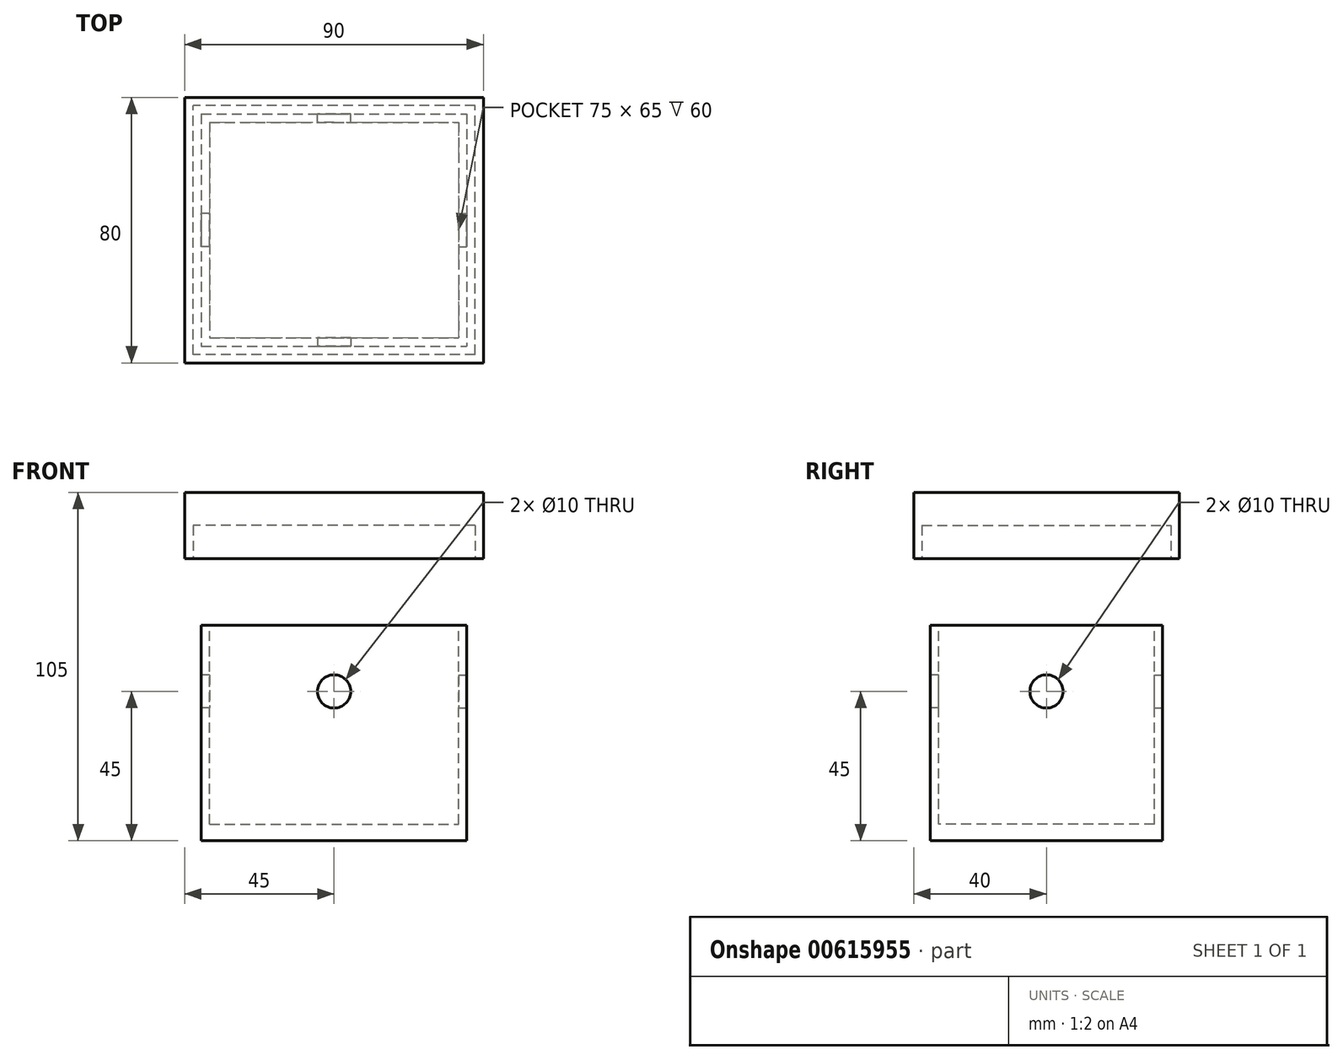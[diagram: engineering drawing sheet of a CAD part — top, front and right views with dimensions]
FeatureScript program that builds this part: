
annotation { "Feature Type Name" : "Feature", "Feature Type Description" : "" }
export const myFeature = defineFeature(function(context is Context, id is Id, definition is map)
    precondition{}
    {
        {
            var Q0;
            Q0=qCreatedBy(makeId("Top.planeOp"),FACE);
            var sketch = newSketch(context, id + "F0", { "sketchPlane" : qUnion([Q0])});
            skLineSegment(sketch, "E0.bottom", {"start": v(-40, 35) * mm, "end": v(40, 35) * mm});
            skLineSegment(sketch, "E0.top", {"start": v(-40, -35) * mm, "end": v(40, -35) * mm});
            skLineSegment(sketch, "E0.left", {"start": v(-40, 35) * mm, "end": v(-40, -35) * mm});
            skLineSegment(sketch, "E0.right", {"start": v(40, 35) * mm, "end": v(40, -35) * mm});
            skPoint(sketch, "E0.middle", {"position": v(0, 0) * mm});
            skLineSegment(sketch, "E1.bottom", {"start": v(-26.5, 26.5) * mm, "end": v(26.5, 26.5) * mm});
            skLineSegment(sketch, "E1.top", {"start": v(-26.5, -26.5) * mm, "end": v(26.5, -26.5) * mm});
            skLineSegment(sketch, "E1.left", {"start": v(-26.5, 26.5) * mm, "end": v(-26.5, -26.5) * mm});
            skLineSegment(sketch, "E1.right", {"start": v(26.5, 26.5) * mm, "end": v(26.5, -26.5) * mm});
            skSolve(sketch);
        }
        {
            var Q0;
            Q0=makeQuery(id+"F0.imprint","IMPRINT",FACE,{"disambiguationData":[TD([[makeQuery(id+"F0.imprint","IMPRINT",EDGE,{"derivedFrom":sQuery(id+"F0.wireOp",EDGE,"E1.bottom")}),-1.0]])]});
            var Q1;
            Q1=makeQuery(id+"F0.imprint","IMPRINT",FACE,{"disambiguationData":[TD([[makeQuery(id+"F0.imprint","IMPRINT",EDGE,{"derivedFrom":sQuery(id+"F0.wireOp",EDGE,"E0.bottom")}),-1.0]])]});
            extrude(context, id + "F1", {"entities" : qUnion([Q0, Q1]), "oppositeDirection" : true, "depth" : 5 * mm, "offsetDistance" : 25 * mm});
        }
        {
            var Q0;
            Q0=makeQuery(id+"F0.imprint","IMPRINT",FACE,{"disambiguationData":[TD([[makeQuery(id+"F0.imprint","IMPRINT",EDGE,{"derivedFrom":sQuery(id+"F0.wireOp",EDGE,"E0.bottom")}),-1.0]])]});
            extrude(context, id + "F2", {"entities" : qUnion([Q0]), "operationType" : NewBodyOperationType.ADD, "depth" : 60 * mm, "offsetDistance" : 25 * mm});
        }
        {
            var Q0;
            Q0=makeQuery(id+"F2.opExtrude","CAP_FACE",FACE,{"disambiguationData":[OSD([sQuery(id+"F0.wireOp",EDGE,"E0.bottom"),sQuery(id+"F0.wireOp",EDGE,"E0.top"),sQuery(id+"F0.wireOp",EDGE,"E0.left"),sQuery(id+"F0.wireOp",EDGE,"E0.right"),sQuery(id+"F0.wireOp",EDGE,"E1.bottom"),sQuery(id+"F0.wireOp",EDGE,"E1.top"),sQuery(id+"F0.wireOp",EDGE,"E1.left"),sQuery(id+"F0.wireOp",EDGE,"E1.right")])],"isStart":false});
            var sketch = newSketch(context, id + "F3", { "sketchPlane" : qUnion([Q0])});
            skLineSegment(sketch, "E2.bottom", {"start": v(45, 40) * mm, "end": v(-45, 40) * mm});
            skLineSegment(sketch, "E2.top", {"start": v(45, -40) * mm, "end": v(-45, -40) * mm});
            skLineSegment(sketch, "E2.left", {"start": v(45, 40) * mm, "end": v(45, -40) * mm});
            skLineSegment(sketch, "E2.right", {"start": v(-45, 40) * mm, "end": v(-45, -40) * mm});
            skPoint(sketch, "E2.middle", {"position": v(0, 0) * mm});
            skSolve(sketch);
        }
        {
            var Q0;
            Q0 = qSketchRegion(id + "F3", true);
            extrude(context, id + "F4", {"entities" : qUnion([Q0]), "operationType" : NewBodyOperationType.ADD, "depth" : 40 * mm, "offsetDistance" : 25 * mm});
        }
        {
            var Q0;
            Q0=makeQuery(id+"F3.imprint","IMPRINT",FACE,{"disambiguationData":[TD([[makeQuery(id+"F3.imprint","IMPRINT",EDGE,{"derivedFrom":sQuery(id+"F3.wireOp",EDGE,"E2.bottom")}),1.0]])]});
            var Q1;
            Q1 = qSketchRegion(id + "F3", true);
            extrude(context, id + "F5", {"entities" : qUnion([Q0, Q1]), "operationType" : NewBodyOperationType.REMOVE, "depth" : 20 * mm, "offsetDistance" : 25 * mm});
        }
        {
            var Q0;
            Q0=makeQuery(id+"F5.boolean.opBoolean","COPY",FACE,{"derivedFrom":makeQuery(id+"F5.opExtrude","CAP_FACE",FACE,{"disambiguationData":[OSD([sQuery(id+"F3.wireOp",EDGE,"E2.bottom"),sQuery(id+"F3.wireOp",EDGE,"E2.top"),sQuery(id+"F3.wireOp",EDGE,"E2.left"),sQuery(id+"F3.wireOp",EDGE,"E2.right")])],"isStart":false})});
            var sketch = newSketch(context, id + "F6", { "sketchPlane" : qUnion([Q0])});
            skLineSegment(sketch, "E3.bottom", {"start": v(42.5, 37.5) * mm, "end": v(-42.5, 37.5) * mm});
            skLineSegment(sketch, "E3.top", {"start": v(42.5, -37.5) * mm, "end": v(-42.5, -37.5) * mm});
            skLineSegment(sketch, "E3.left", {"start": v(42.5, 37.5) * mm, "end": v(42.5, -37.5) * mm});
            skLineSegment(sketch, "E3.right", {"start": v(-42.5, 37.5) * mm, "end": v(-42.5, -37.5) * mm});
            skPoint(sketch, "E3.middle", {"position": v(0, 0) * mm});
            skSolve(sketch);
        }
        {
            var Q0;
            Q0 = qSketchRegion(id + "F6", true);
            extrude(context, id + "F7", {"entities" : qUnion([Q0]), "operationType" : NewBodyOperationType.REMOVE, "oppositeDirection" : true, "depth" : 10 * mm, "offsetDistance" : 25 * mm});
        }
        {
            var Q0;
            Q0=makeQuery(id+"F3.imprint","IMPRINT",FACE,{"disambiguationData":[TD([[makeQuery(id+"F3.imprint","IMPRINT",EDGE,{"derivedFrom":makeQuery(id+"F2.opExtrude","CAP_EDGE",EDGE,{"disambiguationData":[OSD([sQuery(id+"F0.wireOp",EDGE,"E0.bottom")])],"isStart":false})}),-1.0]])]});
            var sketch = newSketch(context, id + "F8", { "sketchPlane" : qUnion([Q0])});
            skLineSegment(sketch, "E4.bottom", {"start": v(-37.5, 32.5) * mm, "end": v(37.5, 32.5) * mm});
            skLineSegment(sketch, "E4.top", {"start": v(-37.5, -32.5) * mm, "end": v(37.5, -32.5) * mm});
            skLineSegment(sketch, "E4.left", {"start": v(-37.5, 32.5) * mm, "end": v(-37.5, -32.5) * mm});
            skLineSegment(sketch, "E4.right", {"start": v(37.5, 32.5) * mm, "end": v(37.5, -32.5) * mm});
            skPoint(sketch, "E4.middle", {"position": v(0, 0) * mm});
            skSolve(sketch);
        }
        {
            var Q0;
            Q0 = qSketchRegion(id + "F8", true);
            extrude(context, id + "F9", {"entities" : qUnion([Q0]), "operationType" : NewBodyOperationType.REMOVE, "oppositeDirection" : true, "depth" : 60 * mm, "offsetDistance" : 25 * mm});
        }
        {
            var Q0;
            {var subQ0=sQuery(id+"F0.wireOp",EDGE,"E0.left");Q0=makeQuery(id+"F2.boolean.opBoolean","MERGE",FACE,{"derivedFrom":[makeQuery(id+"F1.opExtrude","SWEPT_FACE",FACE,{"disambiguationData":[OSD([subQ0])]}),makeQuery(id+"F2.opExtrude","SWEPT_FACE",FACE,{"disambiguationData":[OSD([subQ0])]})]});}
            var sketch = newSketch(context, id + "F10", { "sketchPlane" : qUnion([Q0])});
            skCircle(sketch, "E5", {"center": v(0, 40) * mm, "radius": 5 * mm});
            skLineSegment(sketch, "E6", {"start": v(0, 0) * mm, "end": v(0, 40) * mm});
            skSolve(sketch);
        }
        {
            var Q0;
            Q0 = qSketchRegion(id + "F10", true);
            extrude(context, id + "F11", {"entities" : qUnion([Q0]), "operationType" : NewBodyOperationType.REMOVE, "oppositeDirection" : true, "depth" : 5 * mm, "offsetDistance" : 25 * mm});
        }
        {
            var Q0;
            {var subQ0=sQuery(id+"F0.wireOp",EDGE,"E0.right");Q0=makeQuery(id+"F2.boolean.opBoolean","MERGE",FACE,{"derivedFrom":[makeQuery(id+"F1.opExtrude","SWEPT_FACE",FACE,{"disambiguationData":[OSD([subQ0])]}),makeQuery(id+"F2.opExtrude","SWEPT_FACE",FACE,{"disambiguationData":[OSD([subQ0])]})]});}
            var sketch = newSketch(context, id + "F12", { "sketchPlane" : qUnion([Q0])});
            skLineSegment(sketch, "E7", {"start": v(0, 0) * mm, "end": v(0, 40) * mm});
            skCircle(sketch, "E8", {"center": v(0, 40) * mm, "radius": 5 * mm});
            skSolve(sketch);
        }
        {
            var Q0;
            Q0=makeQuery(id+"F12.imprint","IMPRINT",FACE,{"disambiguationData":[TD([[makeQuery(id+"F12.imprint","IMPRINT",EDGE,{"derivedFrom":sQuery(id+"F12.wireOp",EDGE,"E8")}),1.0]])]});
            var Q1;
            Q1=sQuery(id+"F12.wireOp",EDGE,"hWr7ENGP-HFSW-wkz3-60Nv-MlBUmEK9dnA1");
            extrude(context, id + "F13", {"entities" : qUnion([Q0]), "operationType" : NewBodyOperationType.REMOVE, "surfaceEntities" : qUnion([Q1]), "oppositeDirection" : true, "depth" : 5 * mm, "offsetDistance" : 25 * mm});
        }
        {
            var Q0;
            {var subQ0=sQuery(id+"F0.wireOp",EDGE,"E0.bottom");Q0=makeQuery(id+"F2.boolean.opBoolean","MERGE",FACE,{"derivedFrom":[makeQuery(id+"F1.opExtrude","SWEPT_FACE",FACE,{"disambiguationData":[OSD([subQ0])]}),makeQuery(id+"F2.opExtrude","SWEPT_FACE",FACE,{"disambiguationData":[OSD([subQ0])]})]});}
            var sketch = newSketch(context, id + "F14", { "sketchPlane" : qUnion([Q0])});
            skCircle(sketch, "E9", {"center": v(0, 40) * mm, "radius": 5 * mm});
            skLineSegment(sketch, "E10", {"start": v(0, 0) * mm, "end": v(0, 40) * mm});
            skSolve(sketch);
        }
        {
            var Q0;
            Q0=makeQuery(id+"F14.imprint","IMPRINT",FACE,{"disambiguationData":[TD([[makeQuery(id+"F14.imprint","IMPRINT",EDGE,{"derivedFrom":sQuery(id+"F14.wireOp",EDGE,"E9")}),1.0]])]});
            var Q1;
            Q1=sQuery(id+"F14.wireOp",EDGE,"E9");
            extrude(context, id + "F15", {"entities" : qUnion([Q0]), "operationType" : NewBodyOperationType.REMOVE, "surfaceEntities" : qUnion([Q1]), "oppositeDirection" : true, "depth" : 5 * mm, "offsetDistance" : 25 * mm});
        }
        {
            var Q0;
            {var subQ0=sQuery(id+"F0.wireOp",EDGE,"E0.top");Q0=makeQuery(id+"F2.boolean.opBoolean","MERGE",FACE,{"derivedFrom":[makeQuery(id+"F1.opExtrude","SWEPT_FACE",FACE,{"disambiguationData":[OSD([subQ0])]}),makeQuery(id+"F2.opExtrude","SWEPT_FACE",FACE,{"disambiguationData":[OSD([subQ0])]})]});}
            var sketch = newSketch(context, id + "F16", { "sketchPlane" : qUnion([Q0])});
            skCircle(sketch, "E11", {"center": v(0, 40) * mm, "radius": 5 * mm});
            skLineSegment(sketch, "E12", {"start": v(0, 0) * mm, "end": v(0, 40) * mm});
            skSolve(sketch);
        }
        {
            var Q0;
            Q0=makeQuery(id+"F16.imprint","IMPRINT",FACE,{"disambiguationData":[TD([[makeQuery(id+"F16.imprint","IMPRINT",EDGE,{"derivedFrom":sQuery(id+"F16.wireOp",EDGE,"E11")}),1.0]])]});
            extrude(context, id + "F17", {"entities" : qUnion([Q0]), "operationType" : NewBodyOperationType.REMOVE, "oppositeDirection" : true, "depth" : 5 * mm, "offsetDistance" : 25 * mm});
        }
    });
